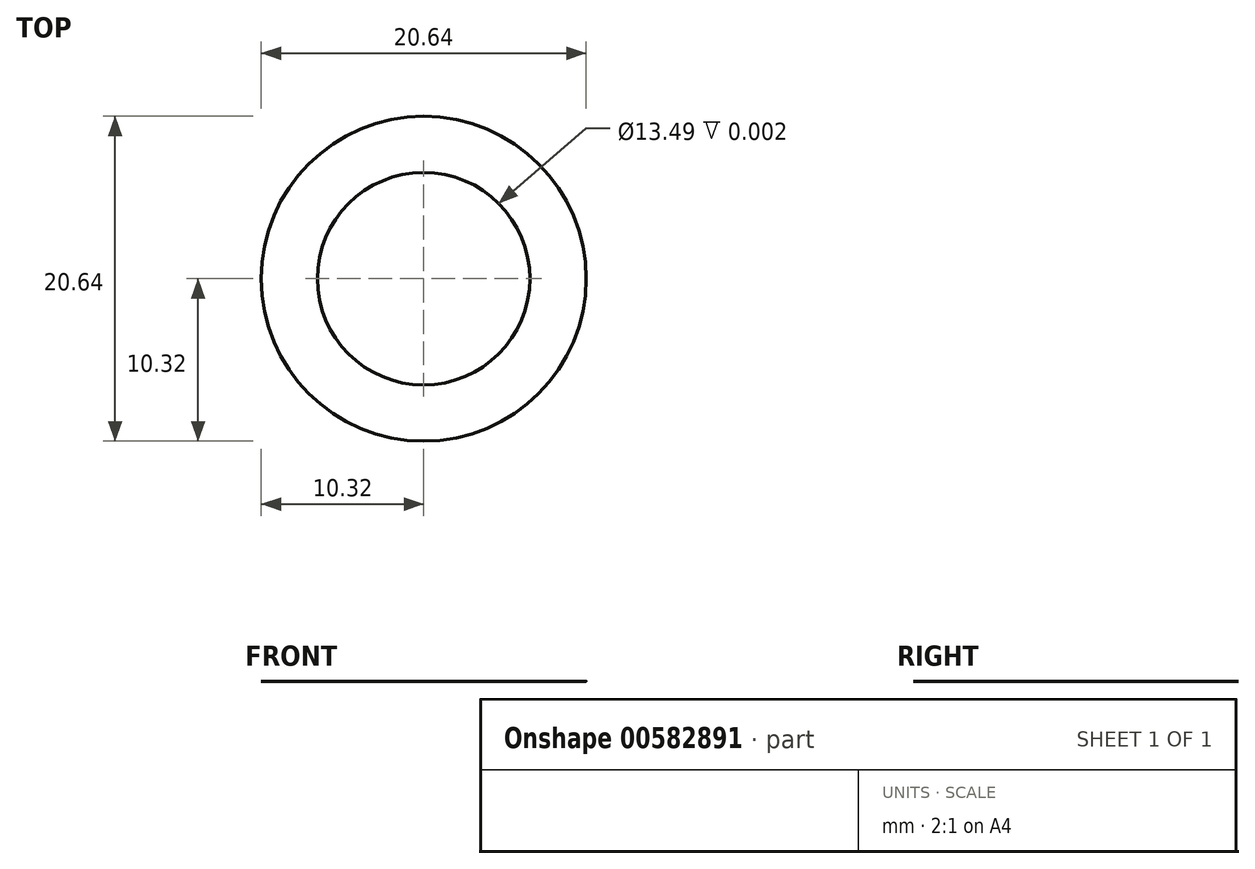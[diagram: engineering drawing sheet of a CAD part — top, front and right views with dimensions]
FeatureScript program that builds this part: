
annotation { "Feature Type Name" : "Feature", "Feature Type Description" : "" }
export const myFeature = defineFeature(function(context is Context, id is Id, definition is map)
    precondition{}
    {
        {
            var Q0;
            Q0=qCreatedBy(makeId("Top.planeOp"),FACE);
            var sketch = newSketch(context, id + "F0", { "sketchPlane" : qUnion([Q0])});
            skCircle(sketch, "E0", {"center": v(0, 0) * mm, "radius": 6.75 * mm});
            skCircle(sketch, "E1", {"center": v(0, 0) * mm, "radius": 10.32 * mm});
            skSolve(sketch);
        }
        {
            var Q0;
            Q0 = qSketchRegion(id + "F0", true);
            extrude(context, id + "F1", {"entities" : qUnion([Q0]), "depth" : 1 / 406.4 * mm, "offsetDistance" : 25.4 * mm});
        }
    });
